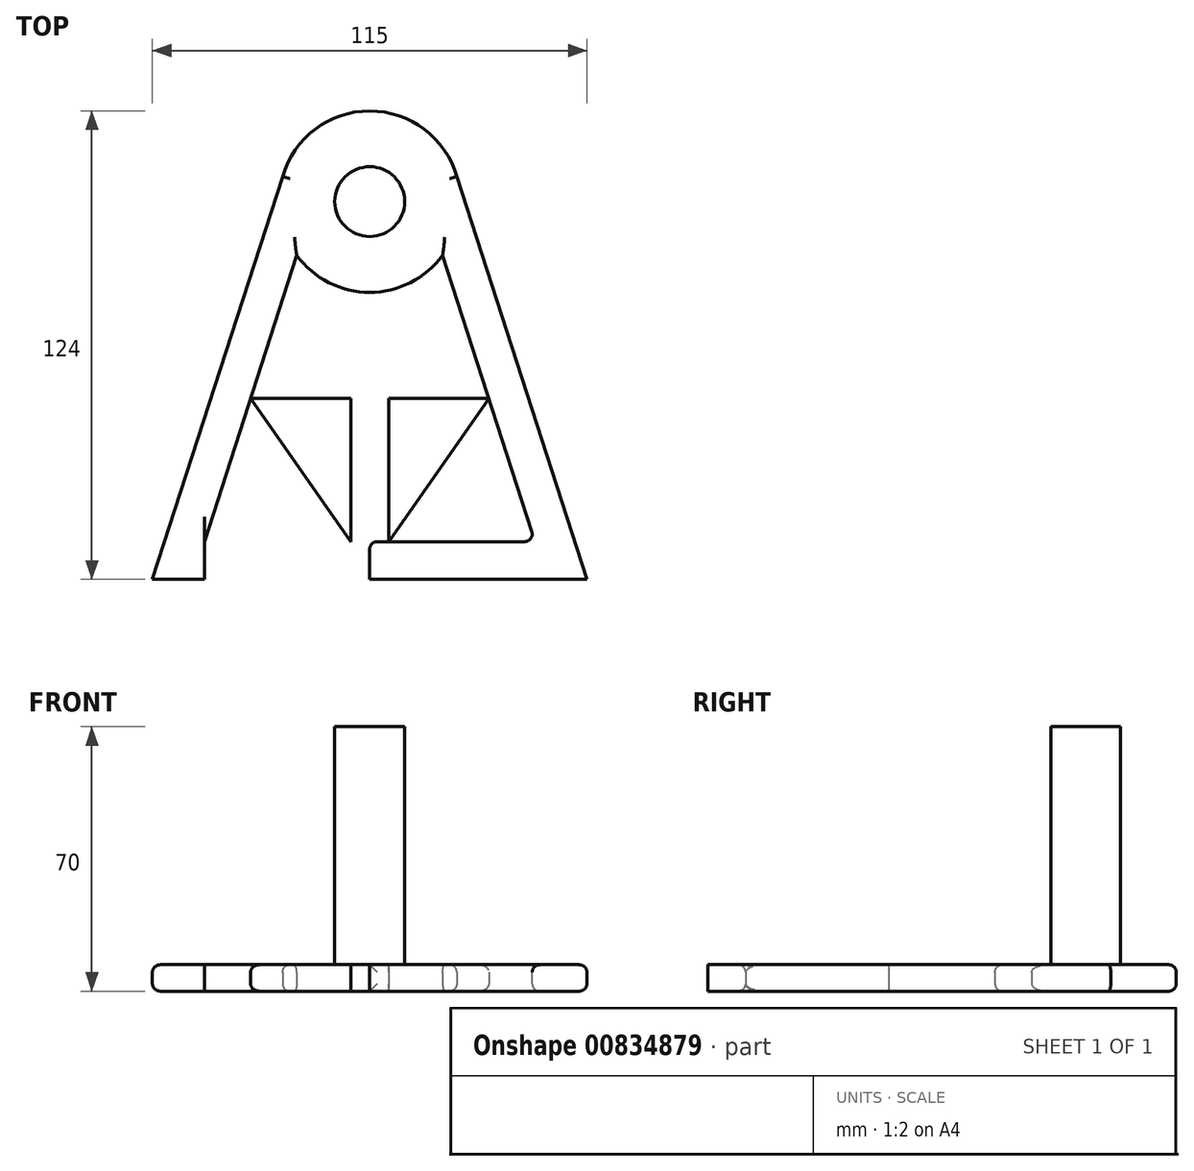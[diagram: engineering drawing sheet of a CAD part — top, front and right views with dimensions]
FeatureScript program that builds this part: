
annotation { "Feature Type Name" : "Feature", "Feature Type Description" : "" }
export const myFeature = defineFeature(function(context is Context, id is Id, definition is map)
    precondition{}
    {
        {
            var Q0;
            Q0=qCreatedBy(makeId("Top.planeOp"),FACE);
            var sketch = newSketch(context, id + "F0", { "sketchPlane" : qUnion([Q0])});
            skCircle(sketch, "E0", {"center": v(3.47, 60.66) * mm, "radius": 14 * mm});
            skLineSegment(sketch, "E1", {"start": v(3.47, 60.66) * mm, "end": v(3.47, -39.34) * mm});
            skCircle(sketch, "E2", {"center": v(3.47, 60.66) * mm, "radius": 24 * mm});
            skLineSegment(sketch, "E3", {"start": v(3.47, -39.34) * mm, "end": v(-54.03, -39.34) * mm});
            skLineSegment(sketch, "E4", {"start": v(-54.03, -39.34) * mm, "end": v(60.97, -39.34) * mm});
            skLineSegment(sketch, "E5", {"start": v(-19.59, 67.32) * mm, "end": v(-54.03, -39.34) * mm});
            skLineSegment(sketch, "E6", {"start": v(26.53, 67.32) * mm, "end": v(60.97, -39.34) * mm});
            skCircle(sketch, "E7", {"center": v(3.47, 60.66) * mm, "radius": 10 * mm});
            skLineSegment(sketch, "E8", {"start": v(28.16, -39.34) * mm, "end": v(28.16, -29.34) * mm});
            skLineSegment(sketch, "E9", {"start": v(28.16, -29.34) * mm, "end": v(-40.29, -29.34) * mm});
            skLineSegment(sketch, "E10", {"start": v(-40.29, -29.34) * mm, "end": v(-49.8, -26.26) * mm});
            skLineSegment(sketch, "E11", {"start": v(-40.29, -29.34) * mm, "end": v(-40.29, -39.34) * mm});
            skLineSegment(sketch, "E12", {"start": v(-40.29, -39.34) * mm, "end": v(-40.29, -29.34) * mm});
            skLineSegment(sketch, "E13", {"start": v(-40.29, -29.34) * mm, "end": v(-15.83, 46.4) * mm});
            skLineSegment(sketch, "E14", {"start": v(28.16, -29.34) * mm, "end": v(47.24, -29.34) * mm});
            skLineSegment(sketch, "E15", {"start": v(47.24, -29.34) * mm, "end": v(56.75, -26.26) * mm});
            skLineSegment(sketch, "E16", {"start": v(47.24, -29.34) * mm, "end": v(22.78, 46.4) * mm});
            skLineSegment(sketch, "E17", {"start": v(-16.36, 44.77) * mm, "end": v(-25.88, 47.84) * mm});
            skLineSegment(sketch, "E18", {"start": v(3.47, -29.34) * mm, "end": v(-1.53, -29.34) * mm});
            skLineSegment(sketch, "E19", {"start": v(-1.53, -29.34) * mm, "end": v(-28.06, 8.53) * mm});
            skLineSegment(sketch, "E20", {"start": v(3.47, -29.34) * mm, "end": v(8.47, -29.34) * mm});
            skLineSegment(sketch, "E21", {"start": v(8.47, -29.34) * mm, "end": v(35, 8.53) * mm});
            skLineSegment(sketch, "E22", {"start": v(8.47, -29.34) * mm, "end": v(8.47, 8.53) * mm});
            skLineSegment(sketch, "E23", {"start": v(-1.53, 8.53) * mm, "end": v(-1.53, -29.34) * mm});
            skLineSegment(sketch, "E24", {"start": v(-1.53, 8.53) * mm, "end": v(-28.06, 8.53) * mm});
            skLineSegment(sketch, "E25", {"start": v(8.47, 8.53) * mm, "end": v(35, 8.53) * mm});
            skLineSegment(sketch, "E26", {"start": v(-1.53, 18.34) * mm, "end": v(-24.9, 18.34) * mm});
            skLineSegment(sketch, "E27", {"start": v(8.47, 18.68) * mm, "end": v(31.73, 18.68) * mm});
            skLineSegment(sketch, "E28", {"start": v(8.47, 18.68) * mm, "end": v(8.47, 37.19) * mm});
            skLineSegment(sketch, "E29", {"start": v(-1.53, 18.34) * mm, "end": v(-1.53, 37.19) * mm});
            skCircle(sketch, "E30", {"center": v(3.47, 60.66) * mm, "radius": 9.25 * mm});
            skSolve(sketch);
        }
        {
            var Q0;
            Q0=makeQuery(id+"F0.imprint","IMPRINT",FACE,{"disambiguationData":[TD([[makeQuery(id+"F0.imprint","IMPRINT",EDGE,{"derivedFrom":sQuery(id+"F0.wireOp",EDGE,"E30")}),1.0]])]});
            extrude(context, id + "F1", {"entities" : qUnion([Q0]), "depth" : 70 * mm, "offsetDistance" : 25 * mm});
        }
        {
            var Q0;
            Q0=makeQuery(id+"F0.imprint","IMPRINT",FACE,{"disambiguationData":[TD([[makeQuery(id+"F0.imprint","IMPRINT",EDGE,{"derivedFrom":sQuery(id+"F0.wireOp",EDGE,"E0")}),-1.0]])]});
            var Q1;
            Q1=makeQuery(id+"F0.imprint","IMPRINT",FACE,{"disambiguationData":[TD([[makeQuery(id+"F0.imprint","IMPRINT",EDGE,{"derivedFrom":sQuery(id+"F0.wireOp",EDGE,"E0")}),1.0]])]});
            var Q2;
            Q2=makeQuery(id+"F0.imprint","IMPRINT",FACE,{"disambiguationData":[TD([[makeQuery(id+"F0.imprint","IMPRINT",EDGE,{"derivedFrom":sQuery(id+"F0.wireOp",EDGE,"E7")}),1.0]])]});
            var Q3;
            {var subQ1=sQuery(id+"F0.wireOp",EDGE,"E15");Q3=makeQuery(id+"F0.imprint","IMPRINT",FACE,{"disambiguationData":[TD([[makeQuery(id+"F0.imprint","IMPRINT",EDGE,{"derivedFrom":subQ1}),1.0]])]});}
            var Q4;
            {var subQ3=sQuery(id+"F0.wireOp",EDGE,"E10");Q4=makeQuery(id+"F0.imprint","IMPRINT",FACE,{"disambiguationData":[TD([[makeQuery(id+"F0.imprint","IMPRINT",EDGE,{"derivedFrom":subQ3}),-1.0]])]});}
            var Q5;
            {var subQ5=sQuery(id+"F0.wireOp",EDGE,"E17");Q5=makeQuery(id+"F0.imprint","IMPRINT",FACE,{"disambiguationData":[TD([[makeQuery(id+"F0.imprint","IMPRINT",EDGE,{"derivedFrom":subQ5}),-1.0]])]});}
            var Q6;
            {var subQ0=sQuery(id+"F0.wireOp",EDGE,"E18");Q6=makeQuery(id+"F0.imprint","IMPRINT",FACE,{"disambiguationData":[TD([[makeQuery(id+"F0.imprint","IMPRINT",EDGE,{"derivedFrom":subQ0}),-1.0]])]});}
            var Q7;
            {var subQ0=sQuery(id+"F0.wireOp",EDGE,"E20");Q7=makeQuery(id+"F0.imprint","IMPRINT",FACE,{"disambiguationData":[TD([[makeQuery(id+"F0.imprint","IMPRINT",EDGE,{"derivedFrom":subQ0}),1.0]])]});}
            var Q8;
            Q8=makeQuery(id+"F0.imprint","IMPRINT",FACE,{"disambiguationData":[TD([[makeQuery(id+"F0.imprint","IMPRINT",EDGE,{"derivedFrom":sQuery(id+"F0.wireOp",EDGE,"E19")}),-1.0]])]});
            var Q9;
            Q9=makeQuery(id+"F0.imprint","IMPRINT",FACE,{"disambiguationData":[TD([[makeQuery(id+"F0.imprint","IMPRINT",EDGE,{"derivedFrom":sQuery(id+"F0.wireOp",EDGE,"E21")}),1.0]])]});
            var Q10;
            {var subQ4=sQuery(id+"F0.wireOp",EDGE,"E8");Q10=makeQuery(id+"F0.imprint","IMPRINT",FACE,{"disambiguationData":[TD([[makeQuery(id+"F0.imprint","IMPRINT",EDGE,{"derivedFrom":subQ4}),-1.0]])]});}
            var Q11;
            {var subQ1=sQuery(id+"F0.wireOp",EDGE,"E8");Q11=makeQuery(id+"F0.imprint","IMPRINT",FACE,{"disambiguationData":[TD([[makeQuery(id+"F0.imprint","IMPRINT",EDGE,{"derivedFrom":subQ1}),1.0]])]});}
            var Q12;
            {var subQ0=sQuery(id+"F0.wireOp",EDGE,"E12");Q12=makeQuery(id+"F0.imprint","IMPRINT",FACE,{"disambiguationData":[TD([[makeQuery(id+"F0.imprint","IMPRINT",EDGE,{"derivedFrom":subQ0}),-1.0]])]});}
            var Q13;
            {var subQ4=sQuery(id+"F0.wireOp",EDGE,"E10");Q13=makeQuery(id+"F0.imprint","IMPRINT",FACE,{"disambiguationData":[TD([[makeQuery(id+"F0.imprint","IMPRINT",EDGE,{"derivedFrom":subQ4}),1.0]])]});}
            extrude(context, id + "F2", {"entities" : qUnion([Q0, Q1, Q2, Q3, Q4, Q5, Q6, Q7, Q8, Q9, Q10, Q11, Q12, Q13]), "operationType" : NewBodyOperationType.ADD, "depth" : 7 * mm, "offsetDistance" : 25 * mm});
        }
        {
            var Q0;
            Q0=makeQuery(id+"F2.opExtrude","CAP_EDGE",EDGE,{"disambiguationData":[OSD([sQuery(id+"F0.wireOp",EDGE,"E29")])],"isStart":false});
            var Q1;
            {var subQ0=sQuery(id+"F0.wireOp",EDGE,"E2");Q1=makeQuery(id+"F2.opExtrude","CAP_EDGE",EDGE,{"disambiguationData":[OSD([subQ0]),TDD([makeQuery(id+"F0.imprint","IMPRINT",EDGE,{"disambiguationData":[TD([[makeQuery(id+"F0.imprint","INTERSECT",VERTEX,{"derivedFrom":[subQ0,sQuery(id+"F0.wireOp",EDGE,"E13")]}),-1.0]])],"derivedFrom":subQ0})])],"isStart":false});}
            var Q2;
            {var subQ0=sQuery(id+"F0.wireOp",EDGE,"E13");var subQ1=makeQuery(id+"F0.imprint","INTERSECT",VERTEX,{"derivedFrom":[subQ0,sQuery(id+"F0.wireOp",EDGE,"E17")]});Q2=makeQuery(id+"F2.opExtrude","CAP_EDGE",EDGE,{"disambiguationData":[OSD([subQ0]),TDD([makeQuery(id+"F0.imprint","IMPRINT",EDGE,{"disambiguationData":[TD([[subQ1,1.0]])],"derivedFrom":subQ0}),makeQuery(id+"F0.imprint","IMPRINT",EDGE,{"disambiguationData":[TD([[makeQuery(id+"F0.imprint","INTERSECT",VERTEX,{"derivedFrom":[sQuery(id+"F0.wireOp",EDGE,"E2"),subQ0]}),1.0]])],"derivedFrom":subQ0})])],"isStart":false});}
            var Q3;
            Q3=makeQuery(id+"F2.opExtrude","CAP_EDGE",EDGE,{"disambiguationData":[OSD([sQuery(id+"F0.wireOp",EDGE,"E26")])],"isStart":false});
            var Q4;
            Q4=makeQuery(id+"F2.opExtrude","CAP_EDGE",EDGE,{"disambiguationData":[OSD([sQuery(id+"F0.wireOp",EDGE,"E27")])],"isStart":false});
            var Q5;
            {var subQ0=sQuery(id+"F0.wireOp",EDGE,"E16");Q5=makeQuery(id+"F2.opExtrude","CAP_EDGE",EDGE,{"disambiguationData":[OSD([subQ0]),TDD([makeQuery(id+"F0.imprint","IMPRINT",EDGE,{"disambiguationData":[TD([[makeQuery(id+"F0.imprint","INTERSECT",VERTEX,{"derivedFrom":[sQuery(id+"F0.wireOp",EDGE,"E2"),subQ0]}),1.0]])],"derivedFrom":subQ0})])],"isStart":false});}
            var Q6;
            {var subQ0=sQuery(id+"F0.wireOp",EDGE,"E2");Q6=makeQuery(id+"F2.opExtrude","CAP_EDGE",EDGE,{"disambiguationData":[OSD([subQ0]),TDD([makeQuery(id+"F0.imprint","IMPRINT",EDGE,{"disambiguationData":[TD([[makeQuery(id+"F0.imprint","INTERSECT",VERTEX,{"derivedFrom":[subQ0,sQuery(id+"F0.wireOp",EDGE,"E16")]}),1.0]])],"derivedFrom":subQ0})])],"isStart":false});}
            var Q7;
            Q7=makeQuery(id+"F2.opExtrude","CAP_EDGE",EDGE,{"disambiguationData":[OSD([sQuery(id+"F0.wireOp",EDGE,"E28")])],"isStart":false});
            var Q8;
            Q8=makeQuery(id+"F2.opExtrude","CAP_EDGE",EDGE,{"disambiguationData":[OSD([sQuery(id+"F0.wireOp",EDGE,"E21")])],"isStart":false});
            var Q9;
            Q9=makeQuery(id+"F2.opExtrude","CAP_EDGE",EDGE,{"disambiguationData":[OSD([sQuery(id+"F0.wireOp",EDGE,"E9"),sQuery(id+"F0.wireOp",EDGE,"E14")])],"isStart":true});
            var Q10;
            {var subQ0=sQuery(id+"F0.wireOp",EDGE,"E16");Q10=makeQuery(id+"F2.opExtrude","CAP_EDGE",EDGE,{"disambiguationData":[OSD([subQ0]),TDD([makeQuery(id+"F0.imprint","IMPRINT",EDGE,{"disambiguationData":[TD([[makeQuery(id+"F0.imprint","INTERSECT",VERTEX,{"derivedFrom":[sQuery(id+"F0.wireOp",EDGE,"E14"),sQuery(id+"F0.wireOp",EDGE,"E15"),subQ0]}),-1.0]])],"derivedFrom":subQ0})])],"isStart":false});}
            var Q11;
            {var subQ0=sQuery(id+"F0.wireOp",EDGE,"E13");Q11=makeQuery(id+"F2.opExtrude","CAP_EDGE",EDGE,{"disambiguationData":[OSD([subQ0]),TDD([makeQuery(id+"F0.imprint","IMPRINT",EDGE,{"disambiguationData":[TD([[makeQuery(id+"F0.imprint","INTERSECT",VERTEX,{"derivedFrom":[subQ0,sQuery(id+"F0.wireOp",EDGE,"E19"),sQuery(id+"F0.wireOp",EDGE,"E24")]}),1.0]])],"derivedFrom":subQ0})])],"isStart":false});}
            var Q12;
            Q12=makeQuery(id+"F2.opExtrude","CAP_EDGE",EDGE,{"disambiguationData":[OSD([sQuery(id+"F0.wireOp",EDGE,"E9")])],"isStart":false});
            var Q13;
            Q13=makeQuery(id+"F2.opExtrude","CAP_EDGE",EDGE,{"disambiguationData":[OSD([sQuery(id+"F0.wireOp",EDGE,"E6")])],"isStart":false});
            var Q14;
            Q14=makeQuery(id+"F2.opExtrude","CAP_EDGE",EDGE,{"disambiguationData":[OSD([sQuery(id+"F0.wireOp",EDGE,"E5")])],"isStart":false});
            var Q15;
            {var subQ0=sQuery(id+"F0.wireOp",EDGE,"E2");Q15=makeQuery(id+"F2.opExtrude","CAP_EDGE",EDGE,{"disambiguationData":[OSD([subQ0]),TDD([makeQuery(id+"F0.imprint","IMPRINT",EDGE,{"disambiguationData":[TD([[makeQuery(id+"F0.imprint","INTERSECT",VERTEX,{"derivedFrom":[subQ0,sQuery(id+"F0.wireOp",EDGE,"E5")]}),1.0]])],"derivedFrom":subQ0})])],"isStart":false});}
            var Q16;
            {var subQ0=sQuery(id+"F0.wireOp",EDGE,"E2");Q16=makeQuery(id+"F2.opExtrude","CAP_EDGE",EDGE,{"disambiguationData":[OSD([subQ0]),TDD([makeQuery(id+"F0.imprint","IMPRINT",EDGE,{"disambiguationData":[TD([[makeQuery(id+"F0.imprint","INTERSECT",VERTEX,{"derivedFrom":[subQ0,sQuery(id+"F0.wireOp",EDGE,"E13")]}),-1.0]])],"derivedFrom":subQ0})])],"isStart":true});}
            var Q17;
            {var subQ0=sQuery(id+"F0.wireOp",EDGE,"E13");var subQ1=makeQuery(id+"F0.imprint","INTERSECT",VERTEX,{"derivedFrom":[subQ0,sQuery(id+"F0.wireOp",EDGE,"E17")]});Q17=makeQuery(id+"F2.opExtrude","CAP_EDGE",EDGE,{"disambiguationData":[OSD([subQ0]),TDD([makeQuery(id+"F0.imprint","IMPRINT",EDGE,{"disambiguationData":[TD([[subQ1,1.0]])],"derivedFrom":subQ0}),makeQuery(id+"F0.imprint","IMPRINT",EDGE,{"disambiguationData":[TD([[makeQuery(id+"F0.imprint","INTERSECT",VERTEX,{"derivedFrom":[sQuery(id+"F0.wireOp",EDGE,"E2"),subQ0]}),1.0]])],"derivedFrom":subQ0})])],"isStart":true});}
            var Q18;
            Q18=makeQuery(id+"F2.opExtrude","CAP_EDGE",EDGE,{"disambiguationData":[OSD([sQuery(id+"F0.wireOp",EDGE,"E29")])],"isStart":true});
            var Q19;
            Q19=makeQuery(id+"F2.opExtrude","CAP_EDGE",EDGE,{"disambiguationData":[OSD([sQuery(id+"F0.wireOp",EDGE,"E26")])],"isStart":true});
            var Q20;
            Q20=makeQuery(id+"F2.opExtrude","CAP_EDGE",EDGE,{"disambiguationData":[OSD([sQuery(id+"F0.wireOp",EDGE,"E28")])],"isStart":true});
            var Q21;
            {var subQ0=sQuery(id+"F0.wireOp",EDGE,"E2");Q21=makeQuery(id+"F2.opExtrude","CAP_EDGE",EDGE,{"disambiguationData":[OSD([subQ0]),TDD([makeQuery(id+"F0.imprint","IMPRINT",EDGE,{"disambiguationData":[TD([[makeQuery(id+"F0.imprint","INTERSECT",VERTEX,{"derivedFrom":[subQ0,sQuery(id+"F0.wireOp",EDGE,"E16")]}),1.0]])],"derivedFrom":subQ0})])],"isStart":true});}
            var Q22;
            {var subQ0=sQuery(id+"F0.wireOp",EDGE,"E16");Q22=makeQuery(id+"F2.opExtrude","CAP_EDGE",EDGE,{"disambiguationData":[OSD([subQ0]),TDD([makeQuery(id+"F0.imprint","IMPRINT",EDGE,{"disambiguationData":[TD([[makeQuery(id+"F0.imprint","INTERSECT",VERTEX,{"derivedFrom":[sQuery(id+"F0.wireOp",EDGE,"E2"),subQ0]}),1.0]])],"derivedFrom":subQ0})])],"isStart":true});}
            var Q23;
            Q23=makeQuery(id+"F2.opExtrude","CAP_EDGE",EDGE,{"disambiguationData":[OSD([sQuery(id+"F0.wireOp",EDGE,"E27")])],"isStart":true});
            var Q24;
            Q24=makeQuery(id+"F2.opExtrude","CAP_EDGE",EDGE,{"disambiguationData":[OSD([sQuery(id+"F0.wireOp",EDGE,"E6")])],"isStart":true});
            var Q25;
            {var subQ0=sQuery(id+"F0.wireOp",EDGE,"E2");Q25=makeQuery(id+"F2.opExtrude","CAP_EDGE",EDGE,{"disambiguationData":[OSD([subQ0]),TDD([makeQuery(id+"F0.imprint","IMPRINT",EDGE,{"disambiguationData":[TD([[makeQuery(id+"F0.imprint","INTERSECT",VERTEX,{"derivedFrom":[subQ0,sQuery(id+"F0.wireOp",EDGE,"E5")]}),1.0]])],"derivedFrom":subQ0})])],"isStart":true});}
            var Q26;
            Q26=makeQuery(id+"F2.opExtrude","CAP_EDGE",EDGE,{"disambiguationData":[OSD([sQuery(id+"F0.wireOp",EDGE,"E19")])],"isStart":false});
            var Q27;
            Q27=makeQuery(id+"F2.opExtrude","CAP_EDGE",EDGE,{"disambiguationData":[OSD([sQuery(id+"F0.wireOp",EDGE,"E19")])],"isStart":true});
            var Q28;
            Q28=makeQuery(id+"F2.opExtrude","CAP_EDGE",EDGE,{"disambiguationData":[OSD([sQuery(id+"F0.wireOp",EDGE,"E9")])],"isStart":true});
            var Q29;
            {var subQ0=sQuery(id+"F0.wireOp",EDGE,"E13");Q29=makeQuery(id+"F2.opExtrude","CAP_EDGE",EDGE,{"disambiguationData":[OSD([subQ0]),TDD([makeQuery(id+"F0.imprint","IMPRINT",EDGE,{"disambiguationData":[TD([[makeQuery(id+"F0.imprint","INTERSECT",VERTEX,{"derivedFrom":[subQ0,sQuery(id+"F0.wireOp",EDGE,"E19"),sQuery(id+"F0.wireOp",EDGE,"E24")]}),1.0]])],"derivedFrom":subQ0})])],"isStart":true});}
            var Q30;
            {var subQ0=sQuery(id+"F0.wireOp",EDGE,"E16");Q30=makeQuery(id+"F2.opExtrude","CAP_EDGE",EDGE,{"disambiguationData":[OSD([subQ0]),TDD([makeQuery(id+"F0.imprint","IMPRINT",EDGE,{"disambiguationData":[TD([[makeQuery(id+"F0.imprint","INTERSECT",VERTEX,{"derivedFrom":[sQuery(id+"F0.wireOp",EDGE,"E14"),sQuery(id+"F0.wireOp",EDGE,"E15"),subQ0]}),-1.0]])],"derivedFrom":subQ0})])],"isStart":true});}
            var Q31;
            Q31=makeQuery(id+"F2.opExtrude","CAP_EDGE",EDGE,{"disambiguationData":[OSD([sQuery(id+"F0.wireOp",EDGE,"E21")])],"isStart":true});
            var Q32;
            Q32=makeQuery(id+"F2.opExtrude","SWEPT_FACE",FACE,{"disambiguationData":[OSD([sQuery(id+"F0.wireOp",EDGE,"E9"),sQuery(id+"F0.wireOp",EDGE,"E14")])]});
            fillet(context, id + "F3", {"entities" : qUnion([Q0, Q1, Q2, Q3, Q4, Q5, Q6, Q7, Q8, Q9, Q10, Q11, Q12, Q13, Q14, Q15, Q16, Q17, Q18, Q19, Q20, Q21, Q22, Q23, Q24, Q25, Q26, Q27, Q28, Q29, Q30, Q31, Q32]), "radius" : 2 * mm, "tangentPropagation" : true, "allowEdgeOverflow" : false});
        }
    });
